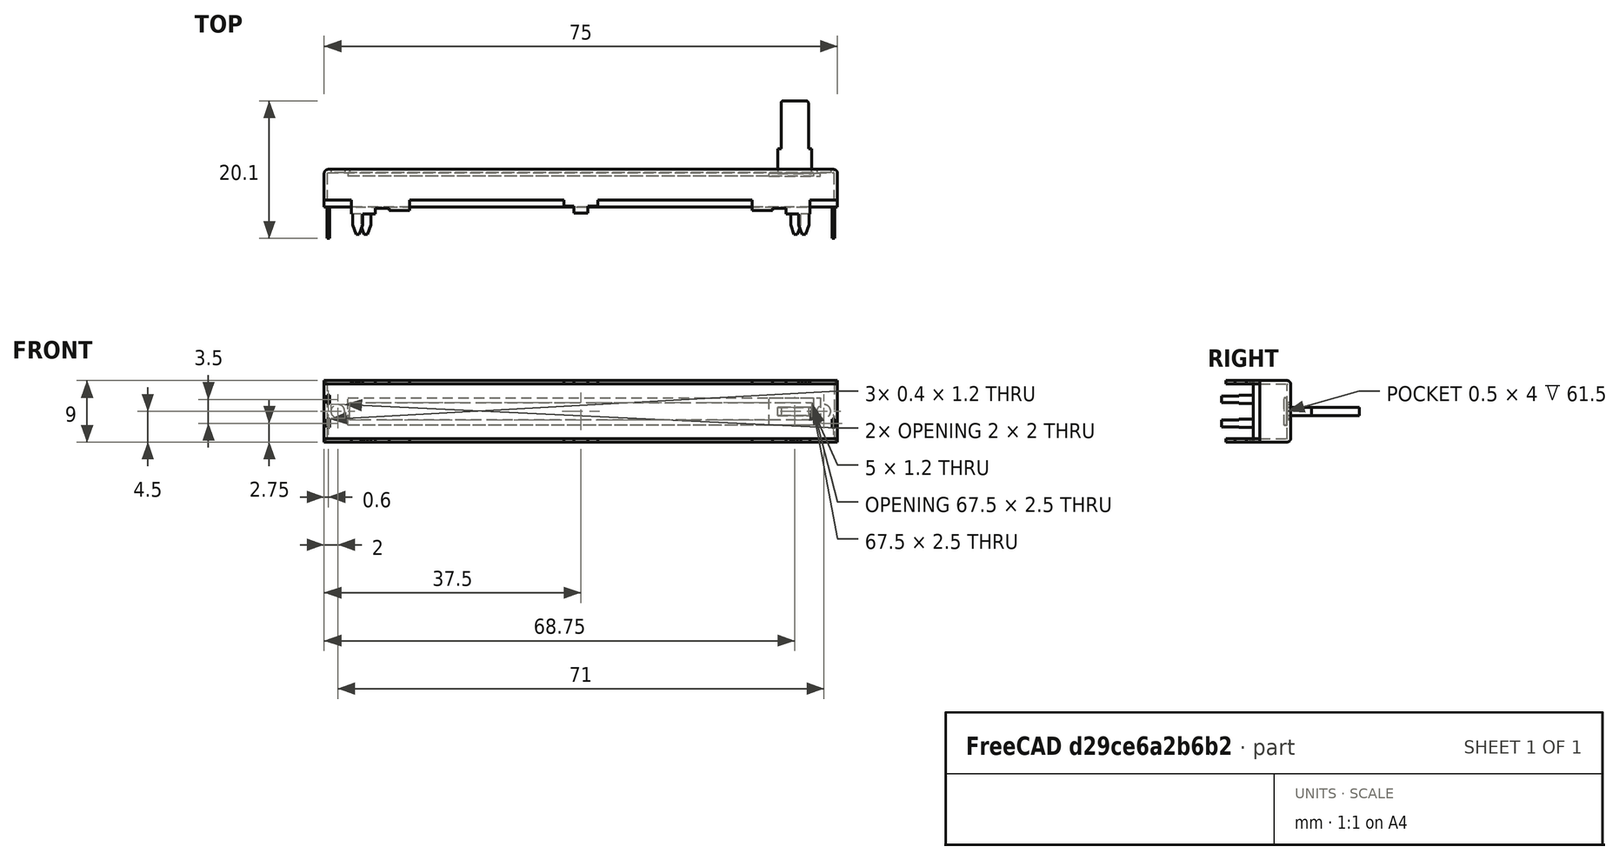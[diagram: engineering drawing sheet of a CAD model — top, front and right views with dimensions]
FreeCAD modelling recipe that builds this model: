
FCSTD DOCUMENT  (FreeCAD 1.0R38641 +468 (Git))
Label: THT-LONGFADER
License: All rights reserved
LicenseURL: https://en.wikipedia.org/wiki/All_rights_reserved
objects: Part::Feature×3, PartDesign::Boolean×1, PartDesign::Body×1
note: 6 computed .brp shape members not serialized (recipe doc carries the construction recipe); baked Part::Feature solids carry a one-line shape summary decoded from their .brp

FEATURE [Part::Feature] Part__Feature  label="BM-517-1"
  shape: bbox 75 x 9.5 x 9 mm, 98 faces (baked)
FEATURE [Part::Feature] Part__Feature001  label="BM-519-1"
  Placement = pos=(0,1,0) rot=(0,0,1;0rad)
  shape: bbox 75 x 9.6 x 8 mm, 46 faces (baked)
FEATURE [Part::Feature] Part__Feature002  label="BM-679"
  Placement = pos=(31.25,5.5,0) rot=(0,0,1;0rad)
  shape: bbox 7.5 x 11 x 4 mm, 17 faces (baked)
FEATURE [PartDesign::Boolean] Boolean
  Group = -> [Part__Feature,Part__Feature001,Part__Feature002]
  Suppressed = false
  Type = 0
  UsePlacement = false
FEATURE [PartDesign::Body] Body  label="THT-LONGFADER"
  AllowCompound = false
  Group = -> [Boolean]
  Origin = -> Origin
  Tip = -> Boolean
